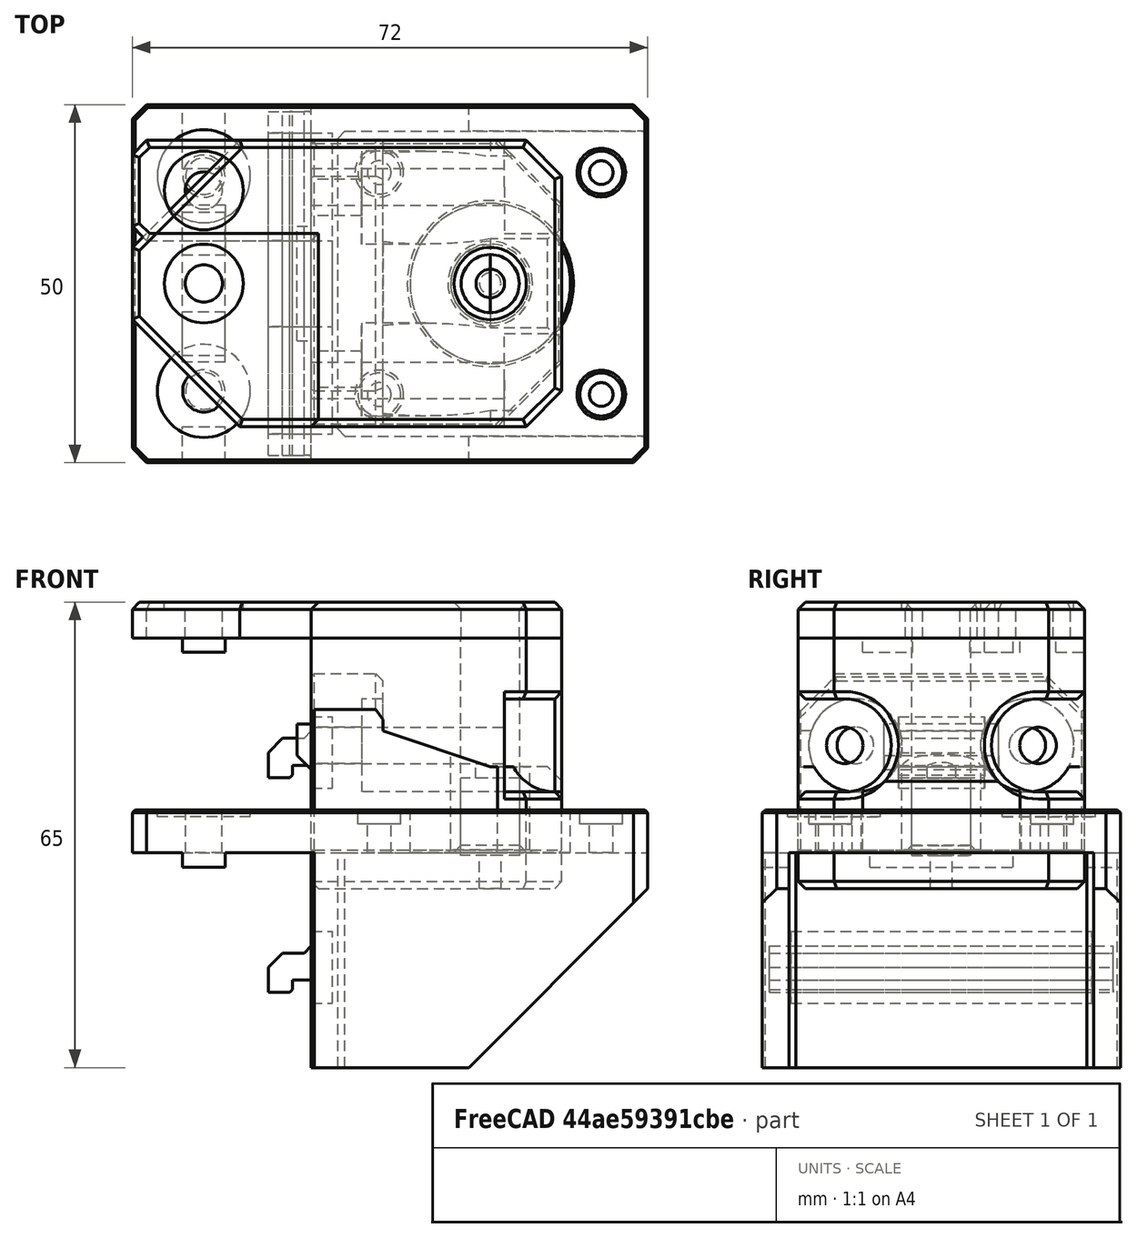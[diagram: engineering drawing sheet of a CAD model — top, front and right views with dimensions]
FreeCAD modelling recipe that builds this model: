
FCSTD DOCUMENT  (FreeCAD 0.18R16146 (Git))
Label: mini-z-mounter
License: All rights reserved
LicenseURL: http://en.wikipedia.org/wiki/All_rights_reserved
objects: Part::Cylinder×32, Part::Chamfer×30, Part::Box×24, Part::MultiFuse×18, Part::Cut×16, Part::Feature×5, Part::MultiCommon×2
note: 127 computed .brp shape members not serialized (recipe doc carries the construction recipe); baked Part::Feature solids carry a one-line shape summary decoded from their .brp

FEATURE [Part::Cylinder] Cylinder001  label="rod-pos-1"
  Angle = 360
  AttacherType = Attacher::AttachEngine3D
  Height = 40
  Placement = pos=(0,0,-0.4) rot=(0,0,1;0rad)
  Radius = 4.05
FEATURE [Part::Box] Box  label="Cube"
  AttacherType = Attacher::AttachEngine3D
  Height = 35
  Length = 35
  Placement = pos=(-25,-20,-5) rot=(0,0,1;0rad)
  Width = 40
FEATURE [Part::Cylinder] Cylinder002
  Angle = 360
  AttacherType = Attacher::AttachEngine3D
  Height = 40
  Placement = pos=(-25,13.5,15) rot=(0,1,0;1.5708rad)
  Radius = 2.55
FEATURE [Part::Cylinder] Cylinder003
  Angle = 360
  AttacherType = Attacher::AttachEngine3D
  Height = 40
  Placement = pos=(-25,-13.5,15) rot=(0,1,0;1.5708rad)
  Radius = 2.55
FEATURE [Part::Cylinder] Cylinder004
  Angle = 360
  AttacherType = Attacher::AttachEngine3D
  Height = 8
  Placement = pos=(2,-13.5,15) rot=(0,1,0;1.5708rad)
  Radius = 6.5
FEATURE [Part::Cylinder] Cylinder005
  Angle = 360
  AttacherType = Attacher::AttachEngine3D
  Height = 8
  Placement = pos=(2,13.5,15) rot=(0,1,0;1.5708rad)
  Radius = 6.5
FEATURE [Part::Box] Box002  label="Cube002"
  AttacherType = Attacher::AttachEngine3D
  Height = 13
  Length = 8
  Placement = pos=(2,13.5,8.5) rot=(0,0,1;0rad)
  Width = 6.5
FEATURE [Part::Box] Box003  label="Cube003"
  AttacherType = Attacher::AttachEngine3D
  Height = 13
  Length = 8
  Placement = pos=(2,-20,8.5) rot=(0,0,1;0rad)
  Width = 6.5
FEATURE [Part::Cylinder] Cylinder
  Angle = 360
  AttacherType = Attacher::AttachEngine3D
  Height = 6
  Radius = 11.2
FEATURE [Part::Cylinder] Cylinder006
  Angle = 360
  AttacherType = Attacher::AttachEngine3D
  Height = 10
  Placement = pos=(-15.5,15.5,0) rot=(0,0,1;0rad)
  Radius = 1.65
FEATURE [Part::Cylinder] Cylinder007
  Angle = 360
  AttacherType = Attacher::AttachEngine3D
  Height = 10
  Placement = pos=(15.5,15.5,0) rot=(0,0,1;0rad)
  Radius = 1.65
FEATURE [Part::Cylinder] Cylinder008
  Angle = 360
  AttacherType = Attacher::AttachEngine3D
  Height = 10
  Placement = pos=(-15.5,-15.5,0) rot=(0,0,1;0rad)
  Radius = 1.65
FEATURE [Part::Cylinder] Cylinder009
  Angle = 360
  AttacherType = Attacher::AttachEngine3D
  Height = 10
  Placement = pos=(15.5,-15.5,0) rot=(0,0,1;0rad)
  Radius = 1.65
FEATURE [Part::Box] Box005  label="Cube005"
  AttacherType = Attacher::AttachEngine3D
  Height = 6
  Length = 72
  Placement = pos=(-50,-25,0) rot=(0,0,1;0rad)
  Width = 50
FEATURE [Part::Box] Box006  label="Cube006"
  AttacherType = Attacher::AttachEngine3D
  Height = 30
  Length = 47
  Placement = pos=(-25,-25,-30) rot=(0,0,1;0rad)
  Width = 3.7
FEATURE [Part::Box] Box007  label="Cube007"
  AttacherType = Attacher::AttachEngine3D
  Height = 30
  Length = 47
  Placement = pos=(-25,21.3,-30) rot=(0,0,1;0rad)
  Width = 3.7
FEATURE [Part::Chamfer] Chamfer005
  Base = -> Box006
  Edges = 1 edges r=25: [Edge8]
FEATURE [Part::Chamfer] Chamfer006
  Base = -> Box007
  Edges = 1 edges r=25: [Edge8]
FEATURE [Part::Box] Box008  label="Cube008"
  AttacherType = Attacher::AttachEngine3D
  Height = 30
  Length = 3.7
  Placement = pos=(-25,-25,-30) rot=(0,0,1;0rad)
  Width = 50
FEATURE [Part::Cylinder] Cylinder010
  Angle = 360
  AttacherType = Attacher::AttachEngine3D
  Height = 2
  Placement = pos=(15.5,15.5,0) rot=(0,0,1;0rad)
  Radius = 3
FEATURE [Part::Cylinder] Cylinder011
  Angle = 360
  AttacherType = Attacher::AttachEngine3D
  Height = 2
  Placement = pos=(-15.5,15.5,0) rot=(0,0,1;0rad)
  Radius = 3
FEATURE [Part::Cylinder] Cylinder012
  Angle = 360
  AttacherType = Attacher::AttachEngine3D
  Height = 2
  Placement = pos=(-15.5,-15.5,0) rot=(0,0,1;0rad)
  Radius = 3
FEATURE [Part::Cylinder] Cylinder013
  Angle = 360
  AttacherType = Attacher::AttachEngine3D
  Height = 2
  Placement = pos=(15.5,-15.5,0) rot=(0,0,1;0rad)
  Radius = 3
FEATURE [Part::MultiFuse] Fusion003
  Placement = pos=(0,0,4) rot=(0,0,1;0rad)
  Shapes = -> [Cylinder013,Cylinder012,Cylinder011,Cylinder010]
FEATURE [Part::Box] Box009  label="Cube009"
  AttacherType = Attacher::AttachEngine3D
  Height = 3.8
  Length = 6
  Placement = pos=(-31,-24,-17.8) rot=(0,0,1;0rad)
  Width = 48
FEATURE [Part::Box] Box010  label="Cube010"
  AttacherType = Attacher::AttachEngine3D
  Height = 2.5
  Length = 3.4
  Placement = pos=(-31,-24,-19.5) rot=(0,0,1;0rad)
  Width = 48
FEATURE [Part::Cylinder] Cylinder014
  Angle = 360
  AttacherType = Attacher::AttachEngine3D
  Height = 10
  Placement = pos=(-40,-15,0) rot=(0,0,1;0rad)
  Radius = 2.55
FEATURE [Part::Cylinder] Cylinder015
  Angle = 360
  AttacherType = Attacher::AttachEngine3D
  Height = 10
  Placement = pos=(-40,15,0) rot=(0,0,1;0rad)
  Radius = 2.55
FEATURE [Part::Cylinder] Cylinder016
  Angle = 360
  AttacherType = Attacher::AttachEngine3D
  Height = 1
  Placement = pos=(-40,15,0) rot=(0,0,1;0rad)
  Radius = 6.5
FEATURE [Part::Cylinder] Cylinder017
  Angle = 360
  AttacherType = Attacher::AttachEngine3D
  Height = 1
  Placement = pos=(-40,-15,0) rot=(0,0,1;0rad)
  Radius = 6.5
FEATURE [Part::MultiFuse] Fusion006
  Placement = pos=(0,0,5) rot=(0,0,1;0rad)
  Shapes = -> [Cylinder016,Cylinder017]
FEATURE [Part::Box] Box012  label="Cube012"
  AttacherType = Attacher::AttachEngine3D
  Height = 2
  Length = 6
  Placement = pos=(-43,-10,-2) rot=(0,0,1;0rad)
  Width = 20
FEATURE [Part::Box] Box013  label="Cube013"
  AttacherType = Attacher::AttachEngine3D
  Height = 2
  Length = 6
  Placement = pos=(-43,-25,-2) rot=(0,0,1;0rad)
  Width = 5
FEATURE [Part::Box] Box014  label="Cube014"
  AttacherType = Attacher::AttachEngine3D
  Height = 2
  Length = 6
  Placement = pos=(-43,20,-2) rot=(0,0,1;0rad)
  Width = 5
FEATURE [Part::MultiFuse] Fusion
  Shapes = -> [Box003,Cylinder004,Cylinder005,Box002,Cylinder002,Cylinder003]
FEATURE [Part::MultiFuse] Fusion012
  Shapes = -> [Cylinder008,Fusion003,Cylinder009,Cylinder006,Cylinder007,Cylinder]
FEATURE [Part::Cut] Cut001
  Base = -> Box005
  Tool = -> Fusion012
FEATURE [Part::Chamfer] Chamfer016
  Base = -> Chamfer005
  Edges = 1 edges r=2: [Edge1]
FEATURE [Part::Chamfer] Chamfer017
  Base = -> Chamfer006
  Edges = 1 edges r=2: [Edge4]
FEATURE [Part::MultiFuse] Fusion013
  Shapes = -> [Chamfer017,Box008,Chamfer016]
FEATURE [Part::Chamfer] Chamfer019
  Base = -> Fusion013
  Edges = 2 edges r=0.4: [Edge1,Edge25]
FEATURE [Part::Chamfer] Chamfer020
  Base = -> Box010
  Edges = 1 edges r=0.4: [Edge8]
FEATURE [Part::Chamfer] Chamfer021
  Base = -> Box009
  Edges = 1 edges r=2: [Edge2]
FEATURE [Part::MultiFuse] Fusion014
  Shapes = -> [Chamfer021,Chamfer020]
FEATURE [Part::Chamfer] Chamfer023
  Base = -> Chamfer019
  Edges = 2 edges r=1: [Edge35,Edge36]
FEATURE [Part::Cylinder] Cylinder018  label="rod-pos-002"
  Angle = 360
  AttacherType = Attacher::AttachEngine3D
  Height = 10.4
  Radius = 4.1
FEATURE [Part::Cylinder] Cylinder019  label="leadscrew-pos"
  Angle = 360
  AttacherType = Attacher::AttachEngine3D
  Height = 40
  Radius = 5.5
FEATURE [Part::Box] Box015  label="Cube015"
  AttacherType = Attacher::AttachEngine3D
  Height = 12
  Length = 35
  Placement = pos=(-25,-20,0) rot=(0,0,1;0rad)
  Width = 40
FEATURE [Part::Box] Box016  label="Cube016"
  AttacherType = Attacher::AttachEngine3D
  Height = 25
  Length = 10
  Placement = pos=(-25,-20,0) rot=(0,0,1;0rad)
  Width = 40
FEATURE [Part::Box] Box017  label="Cube017"
  AttacherType = Attacher::AttachEngine3D
  Height = 6.4
  Length = 3
  Placement = pos=(-27,-8,11.6) rot=(0,0,1;0rad)
  Width = 16
FEATURE [Part::Cylinder] Cylinder020  label="Cylinder018"
  Angle = 360
  AttacherType = Attacher::AttachEngine3D
  Height = 30
  Placement = pos=(10,-12,15) rot=(0,-1,0;1.5708rad)
  Radius = 6.5
FEATURE [Part::Cylinder] Cylinder021  label="Cylinder019"
  Angle = 360
  AttacherType = Attacher::AttachEngine3D
  Height = 30
  Placement = pos=(10,12,15) rot=(0,-1,0;1.5708rad)
  Radius = 6.5
FEATURE [Part::Cylinder] Cylinder022  label="Cylinder020"
  Angle = 360
  AttacherType = Attacher::AttachEngine3D
  Height = 40
  Placement = pos=(10,-12,15) rot=(0,-1,0;1.5708rad)
  Radius = 2.55
FEATURE [Part::Cylinder] Cylinder023  label="Cylinder021"
  Angle = 360
  AttacherType = Attacher::AttachEngine3D
  Height = 40
  Placement = pos=(10,12,15) rot=(0,-1,0;1.5708rad)
  Radius = 2.55
FEATURE [Part::MultiFuse] Fusion016
  Placement = pos=(2,0,0) rot=(0,0,1;0rad)
  Shapes = -> [Cylinder021,Cylinder020]
FEATURE [Part::MultiFuse] Fusion018
  Shapes = -> [Cylinder022,Cylinder023]
FEATURE [Part::MultiFuse] Fusion019
  Shapes = -> [Box016,Box015]
FEATURE [Part::Chamfer] Chamfer025
  Base = -> Fusion019
  Edges = 1 edges: [Edge28 r1=15 r2=5]
FEATURE [Part::Chamfer] Chamfer026
  Base = -> Chamfer025
  Edges = 2 edges r=5: [Edge11,Edge27]
FEATURE [Part::Chamfer] Chamfer027
  Base = -> Chamfer026
  Edges = 2 edges r=9: [Edge21,Edge34]
FEATURE [Part::Chamfer] Chamfer028
  Base = -> Chamfer027
  Edges = 15 edges r=0.4: [Edge4,Edge11,Edge16,Edge18,Edge19,Edge21,Edge22,Edge23,Edge34,Edge37,Edge38,Edge39,Edge40,Edge41,Edge42]
FEATURE [Part::Cut] Cut003
  Base = -> Chamfer028
  Tool = -> Fusion016
FEATURE [Part::Cut] Cut004
  Base = -> Cut003
  Tool = -> Fusion018
FEATURE [Part::Chamfer] Chamfer029
  Base = -> Cut004
  Edges = 1 edges r=2: [Edge25]
FEATURE [Part::Chamfer] Chamfer030
  Base = -> Chamfer029
  Edges = 3 edges r=1: [Edge43,Edge44,Edge45]
FEATURE [Part::MultiFuse] Fusion020003
  Shapes = -> [Cylinder015,Cylinder014]
FEATURE [Part::Cut] Cut009
  Base = -> Cut001
  Tool = -> Fusion020003
FEATURE [Part::MultiFuse] Fusion020004
  Shapes = -> [Chamfer023,Fusion014]
FEATURE [Part::Chamfer] Chamfer033003
  Base = -> Fusion020004
  Edges = 1 edges r=1: [Edge30]
FEATURE [Part::Chamfer] Chamfer033004
  Base = -> Cut009
  Edges = 4 edges r=2: [Edge1,Edge3,Edge6,Edge18]
FEATURE [Part::MultiFuse] Fusion020005
  Shapes = -> [Box014,Box012,Box013]
FEATURE [Part::Chamfer] Chamfer033005
  Base = -> Chamfer033004
  Edges = 15 edges r=0.4: [Edge1,Edge5,Edge6,Edge7,Edge8,Edge9,Edge10,Edge11,Edge12,Edge13,Edge14,Edge15,Edge16,Edge17,Edge18]
FEATURE [Part::MultiFuse] Fusion020006  label="motor-mount-r2"
  Shapes = -> [Chamfer033005,Fusion020005,Chamfer033003]
FEATURE [Part::Cut] Cut
  Base = -> Box
  Tool = -> Fusion
FEATURE [Part::Cylinder] Cylinder024  label="rod-pos-003"
  Angle = 360
  AttacherType = Attacher::AttachEngine3D
  Height = 40
  Placement = pos=(0,0,-15) rot=(0,0,1;0rad)
  Radius = 1.5
FEATURE [Part::Cut] Cut010
  Base = -> Cut
  Tool = -> Cylinder024
FEATURE [Part::Box] Box018  label="Cube018"
  AttacherType = Attacher::AttachEngine3D
  Height = 5
  Length = 60
  Placement = pos=(-50,-20,30) rot=(0,0,1;0rad)
  Width = 40
FEATURE [Part::Chamfer] Chamfer
  Base = -> Cut010
  Edges = 4 edges r=5: [Edge7,Edge12,Edge20,Edge25]
FEATURE [Part::Chamfer] Chamfer033006
  Base = -> Chamfer
  Edges = 14 edges r=1: [Edge1,Edge7,Edge10,Edge11,Edge28,Edge29,Edge36,Edge38,Edge39,Edge41,Edge46,Edge50,Edge52,Edge60]
FEATURE [Part::Box] Box019  label="Cube019"
  AttacherType = Attacher::AttachEngine3D
  Height = 5
  Length = 60
  Placement = pos=(-50,-20,30) rot=(0,0,1;0rad)
  Width = 40
FEATURE [Part::Chamfer] Chamfer033009
  Base = -> Box019
  Edges = 2 edges r=5: [Edge5,Edge7]
FEATURE [Part::Cylinder] Cylinder025  label="Cylinder022"
  Angle = 360
  AttacherType = Attacher::AttachEngine3D
  Height = 10
  Placement = pos=(-40,0,28) rot=(0,0,1;0rad)
  Radius = 2.6
FEATURE [Part::Chamfer] Chamfer033010
  Base = -> Chamfer033009
  Edges = 2 edges r=15: [Edge17,Edge18]
FEATURE [Part::Cylinder] Cylinder026  label="Cylinder023"
  Angle = 360
  AttacherType = Attacher::AttachEngine3D
  Height = 2
  Placement = pos=(-40,0,34) rot=(0,0,1;0rad)
  Radius = 5.5
FEATURE [Part::Chamfer] Chamfer033011
  Base = -> Chamfer033010
  Edges = 8 edges r=1: [Edge1,Edge2,Edge3,Edge4,Edge5,Edge6,Edge7,Edge8]
FEATURE [Part::Cylinder] Cylinder027  label="rod-pos-004"
  Angle = 360
  AttacherType = Attacher::AttachEngine3D
  Height = 40
  Placement = pos=(0,0,-0.4) rot=(0,0,1;0rad)
  Radius = 4.1
FEATURE [Part::Cut] Cut011
  Base = -> Chamfer033011
  Tool = -> Cylinder001
FEATURE [Part::Chamfer] Chamfer033012
  Base = -> Cut011
  Edges = 1 edges r=1: [Edge9]
FEATURE [Part::Cut] Cut012
  Base = -> Chamfer033012
  Tool = -> Cylinder026
FEATURE [Part::Cut] Cut013  label="rod-center-cap"
  Base = -> Cut012
  Tool = -> Cylinder025
FEATURE [Part::Chamfer] Chamfer033013
  Base = -> Chamfer033006
  Edges = 6 edges r=1: [Edge3,Edge13,Edge18,Edge19,Edge20,Edge21]
FEATURE [Part::Cylinder] Cylinder028  label="rod-pos-005"
  Angle = 360
  AttacherType = Attacher::AttachEngine3D
  Height = 40
  Placement = pos=(0,0,-0.4) rot=(0,0,1;0rad)
  Radius = 4.05
FEATURE [Part::Box] Box020  label="Cube020"
  AttacherType = Attacher::AttachEngine3D
  Height = 5
  Length = 25
  Placement = pos=(-50,-20,30) rot=(0,0,1;0rad)
  Width = 26
FEATURE [Part::Cut] Cut015
  Base = -> Box018
  Tool = -> Box020
FEATURE [Part::Chamfer] Chamfer033014
  Base = -> Cut015
  Edges = 2 edges r=5: [Edge13,Edge18]
FEATURE [Part::Cut] Cut016
  Base = -> Chamfer033014
  Tool = -> Cylinder028
FEATURE [Part::Cylinder] Cylinder029  label="Cylinder024"
  Angle = 360
  AttacherType = Attacher::AttachEngine3D
  Height = 10
  Placement = pos=(-40,13,29) rot=(0,0,1;0rad)
  Radius = 2.6
FEATURE [Part::Cylinder] Cylinder030  label="Cylinder025"
  Angle = 360
  AttacherType = Attacher::AttachEngine3D
  Height = 3
  Placement = pos=(-40,13,34) rot=(0,0,1;0rad)
  Radius = 5.5
FEATURE [Part::MultiFuse] Fusion020008
  Shapes = -> [Cylinder030,Cylinder029]
FEATURE [Part::Chamfer] Chamfer033015
  Base = -> Cut016
  Edges = 2 edges r=2: [Edge12,Edge15]
FEATURE [Part::Cut] Cut017
  Base = -> Chamfer033015
  Tool = -> Fusion020008
FEATURE [Part::Chamfer] Chamfer033016  label="rod-corner-cap"
  Base = -> Cut017
  Edges = 11 edges r=1: [Edge1,Edge2,Edge3,Edge4,Edge5,Edge6,Edge7,Edge8,Edge9,Edge10,Edge11]
FEATURE [Part::Feature] Fusion020006001  label="motor-mount-r003"
  shape: bbox 72 x 50 x 36 mm, 100 faces (baked)
FEATURE [Part::Box] Box021  label="Cube021"
  AttacherType = Attacher::AttachEngine3D
  Height = 10
  Length = 10
  Placement = pos=(-32,-21,-21) rot=(0,0,1;0rad)
  Width = 42
FEATURE [Part::MultiCommon] Common  label="rev-hook"
  Shapes = -> [Box021,Fusion020006001]
FEATURE [Part::Feature] Common001  label="rev-hook001"
  Placement = pos=(0,0,30) rot=(0,0,1;0rad)
  shape: bbox 9 x 42 x 10 mm, 15 faces (baked)
FEATURE [Part::Box] Box022  label="Cube022"
  AttacherType = Attacher::AttachEngine3D
  Height = 22
  Length = 10
  Placement = pos=(-32,-6,0) rot=(0,0,1;0rad)
  Width = 12
FEATURE [Part::Box] Box023  label="Cube023"
  AttacherType = Attacher::AttachEngine3D
  Height = 3
  Length = 6
  Placement = pos=(-43,4,28) rot=(0,0,1;0rad)
  Width = 7
FEATURE [Part::Box] Box024  label="Cube024"
  AttacherType = Attacher::AttachEngine3D
  Height = 3
  Length = 6
  Placement = pos=(-43,-11,28) rot=(0,0,1;0rad)
  Width = 7
FEATURE [Part::Box] Box025  label="Cube025"
  AttacherType = Attacher::AttachEngine3D
  Height = 3
  Length = 6
  Placement = pos=(-43,16,28) rot=(0,0,1;0rad)
  Width = 4
FEATURE [Part::Box] Box026  label="Cube026"
  AttacherType = Attacher::AttachEngine3D
  Height = 3
  Length = 6
  Placement = pos=(-43,6,28) rot=(0,0,1;0rad)
  Width = 4
FEATURE [Part::MultiCommon] Common002
  Shapes = -> [Box022,Common001]
FEATURE [Part::Feature] Common002001  label="Common003"
  shape: bbox 9 x 12 x 10 mm, 15 faces (baked)
FEATURE [Part::MultiFuse] Fusion020006005  label="rod-corner-cap-r1"
  Shapes = -> [Chamfer033016,Box026,Box025]
FEATURE [Part::MultiFuse] Fusion020006006  label="rod-center-cap001"
  Shapes = -> [Box023,Cut013,Box024]
FEATURE [Part::Chamfer] Chamfer033017
  Base = -> Box017
  Edges = 1 edges r=2: [Edge4]
FEATURE [Part::MultiFuse] Fusion020006007  label="top-mount-base"
  Shapes = -> [Chamfer030,Chamfer033017]
FEATURE [Part::Feature] Fusion020006007001  label="top-mount-base003"
  shape: bbox 37 x 40 x 25 mm, 45 faces (baked)
FEATURE [Part::Cut] Cut018
  Base = -> Fusion020006007001
  Tool = -> Cylinder019
FEATURE [Part::Chamfer] Chamfer033018  label="lead-screw-mount-r1"
  Base = -> Cut018
  Edges = 1 edges r=0.4: [Edge85]
FEATURE [Part::Feature] Fusion020006007002  label="top-mount-base004"
  shape: bbox 37 x 40 x 25 mm, 55 faces (baked)
FEATURE [Part::Cylinder] Cylinder031  label="rod-pos-006"
  Angle = 360
  AttacherType = Attacher::AttachEngine3D
  Height = 17.4
  Radius = 2
FEATURE [Part::Cut] Cut019
  Base = -> Fusion020006007002
  Tool = -> Cylinder018
FEATURE [Part::Cut] Cut020
  Base = -> Cut019
  Tool = -> Cylinder031
FEATURE [Part::Chamfer] Chamfer033019  label="rod-cap-r1-f1"
  Base = -> Cut020
  Edges = 1 edges r=1: [Edge139]
FEATURE [Part::Cut] Cut021
  Base = -> Chamfer033013
  Tool = -> Cylinder027
FEATURE [Part::MultiFuse] Fusion020006007003  label="rod-mount-base"
  Shapes = -> [Common002,Cut021]
